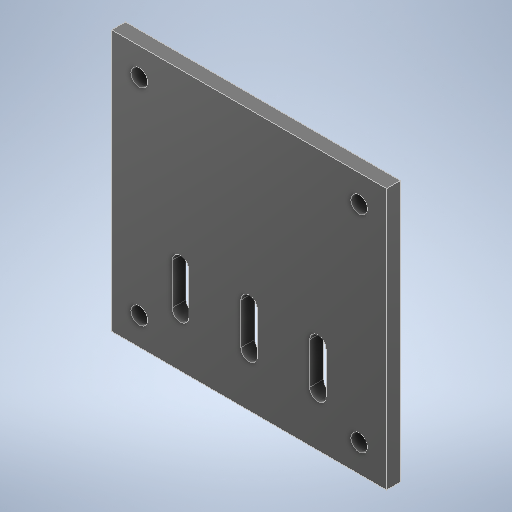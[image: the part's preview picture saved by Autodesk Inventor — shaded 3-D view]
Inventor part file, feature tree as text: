
AUTODESK INVENTOR PART (.ipt)
format: ipt  version: 2025.1 (Build 291241020, 241B)  size: 587,776 bytes
history: native  units: mm
features: sketch x2, extrude x2, hole x1
ambient origin geometry x8: Origin, YZ Plane, XZ Plane, XY Plane, X Axis, Y Axis, Z Axis, Center Point
bodies: Solid1 (feature_tree)
feature tree (5):
  sketch  "Sketch1"  dims[d0=100.0mm d1=95.0mm]
  extrude  "Extrusion1"  Depth=95.0mm
  hole  "Hole1"  [1 undecoded]
  extrude  "Extrusion2"  Depth=10.0mm
  sketch  "Sketch2"  dims[d2=5.0mm d3=0.0mm d4=75.0mm d5=10.0mm d6=80.0mm d7=10.0mm d8=6.0mm d9=6.0mm d10=4.0mm d11=2.0mm d12=90.0deg d13=8.0mm d14=20.594885mm d15=50.0mm d17=25.0mm d18=25.0mm d19=69.099mm d27=6.0mm d28=15.0mm d29=7.5mm d30=10.0mm d31=0.0mm]
note: 1 required parameter value undecoded (feature->parameter linkage not recoverable at this tier; creation-order binding heuristic only, values carry confidence <= 0.55)
